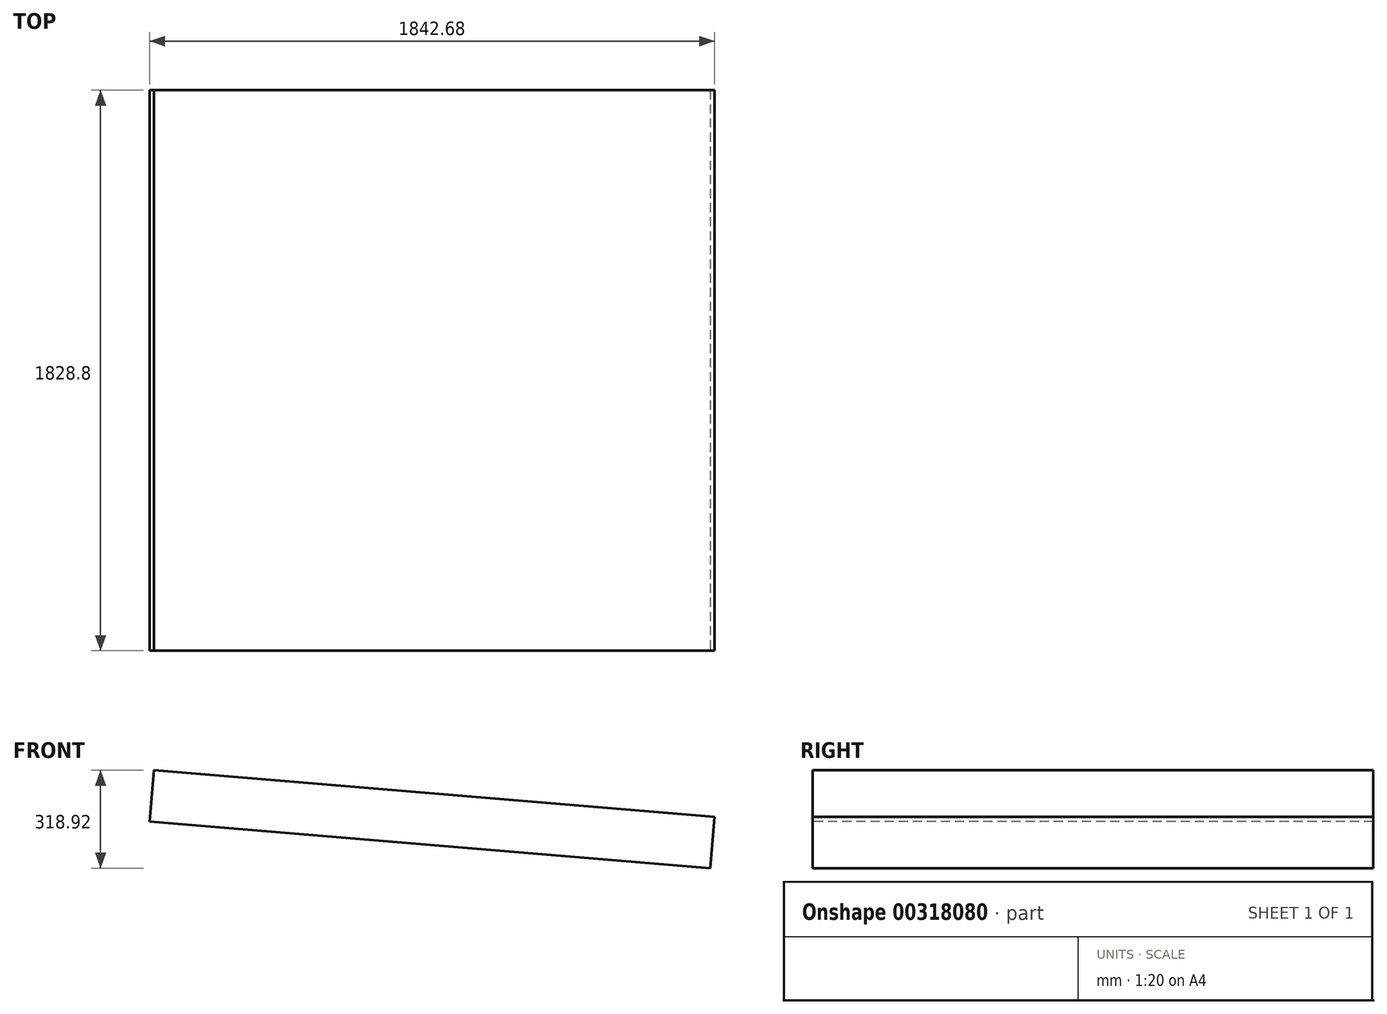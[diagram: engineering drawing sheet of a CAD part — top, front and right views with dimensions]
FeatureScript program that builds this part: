
annotation { "Feature Type Name" : "Feature", "Feature Type Description" : "" }
export const myFeature = defineFeature(function(context is Context, id is Id, definition is map)
    precondition{}
    {
        {
            var Q0;
            Q0=qCreatedBy(makeId("Top.planeOp"),FACE);
            var sketch = newSketch(context, id + "F0", { "sketchPlane" : qUnion([Q0])});
            skLineSegment(sketch, "E0.bottom", {"start": v(914.4, 914.4) * mm, "end": v(-914.4, 914.4) * mm});
            skLineSegment(sketch, "E0.top", {"start": v(914.4, -914.4) * mm, "end": v(-914.4, -914.4) * mm});
            skLineSegment(sketch, "E0.left", {"start": v(914.4, 914.4) * mm, "end": v(914.4, -914.4) * mm});
            skLineSegment(sketch, "E0.right", {"start": v(-914.4, 914.4) * mm, "end": v(-914.4, -914.4) * mm});
            skPoint(sketch, "E0.middle", {"position": v(0, 0) * mm});
            skSolve(sketch);
        }
        {
            var Q0;
            Q0 = qSketchRegion(id + "F0", true);
            extrude(context, id + "F1", {"entities" : qUnion([Q0]), "depth" : 152.4 * mm});
        }
        {
            var Q0;
            Q0=makeQuery(id+"F1.opExtrude","SWEPT_FACE",FACE,{"disambiguationData":[OSD([sQuery(id+"F0.wireOp",EDGE,"E0.top")])]});
            var sketch = newSketch(context, id + "F2", { "sketchPlane" : qUnion([Q0])});
            skLineSegment(sketch, "E1", {"start": v(-914.4, 152.4) * mm, "end": v(914.4, 0) * mm});
            skLineSegment(sketch, "E2", {"start": v(914.4, 0) * mm, "end": v(900.52, -166.52) * mm});
            skLineSegment(sketch, "E3", {"start": v(900.52, -166.52) * mm, "end": v(-928.28, -14.12) * mm});
            skLineSegment(sketch, "E4", {"start": v(-928.28, -14.12) * mm, "end": v(-914.4, 152.4) * mm});
            skSolve(sketch);
        }
        {
            var Q0;
            Q0=makeQuery(id+"F2.imprint","IMPRINT",FACE,{"disambiguationData":[TD([[makeQuery(id+"F2.imprint","IMPRINT",EDGE,{"derivedFrom":sQuery(id+"F2.wireOp",EDGE,"E1")}),1.0]])]});
            extrude(context, id + "F3", {"entities" : qUnion([Q0]), "operationType" : NewBodyOperationType.REMOVE, "endBound" : BoundingType.THROUGH_ALL, "oppositeDirection" : true, "depth" : 25 * mm});
        }
        {
            var Q0;
            Q0 = qSketchRegion(id + "F2", true);
            var Q1;
            Q1=makeQuery(id+"F1.opExtrude","SWEPT_FACE",FACE,{"disambiguationData":[OSD([sQuery(id+"F0.wireOp",EDGE,"E0.bottom")])]});
            extrude(context, id + "F4", {"entities" : qUnion([Q0]), "operationType" : NewBodyOperationType.ADD, "endBound" : BoundingType.UP_TO_SURFACE, "oppositeDirection" : true, "endBoundEntityFace" : qUnion([Q1]), "depth" : 25 * mm});
        }
    });
